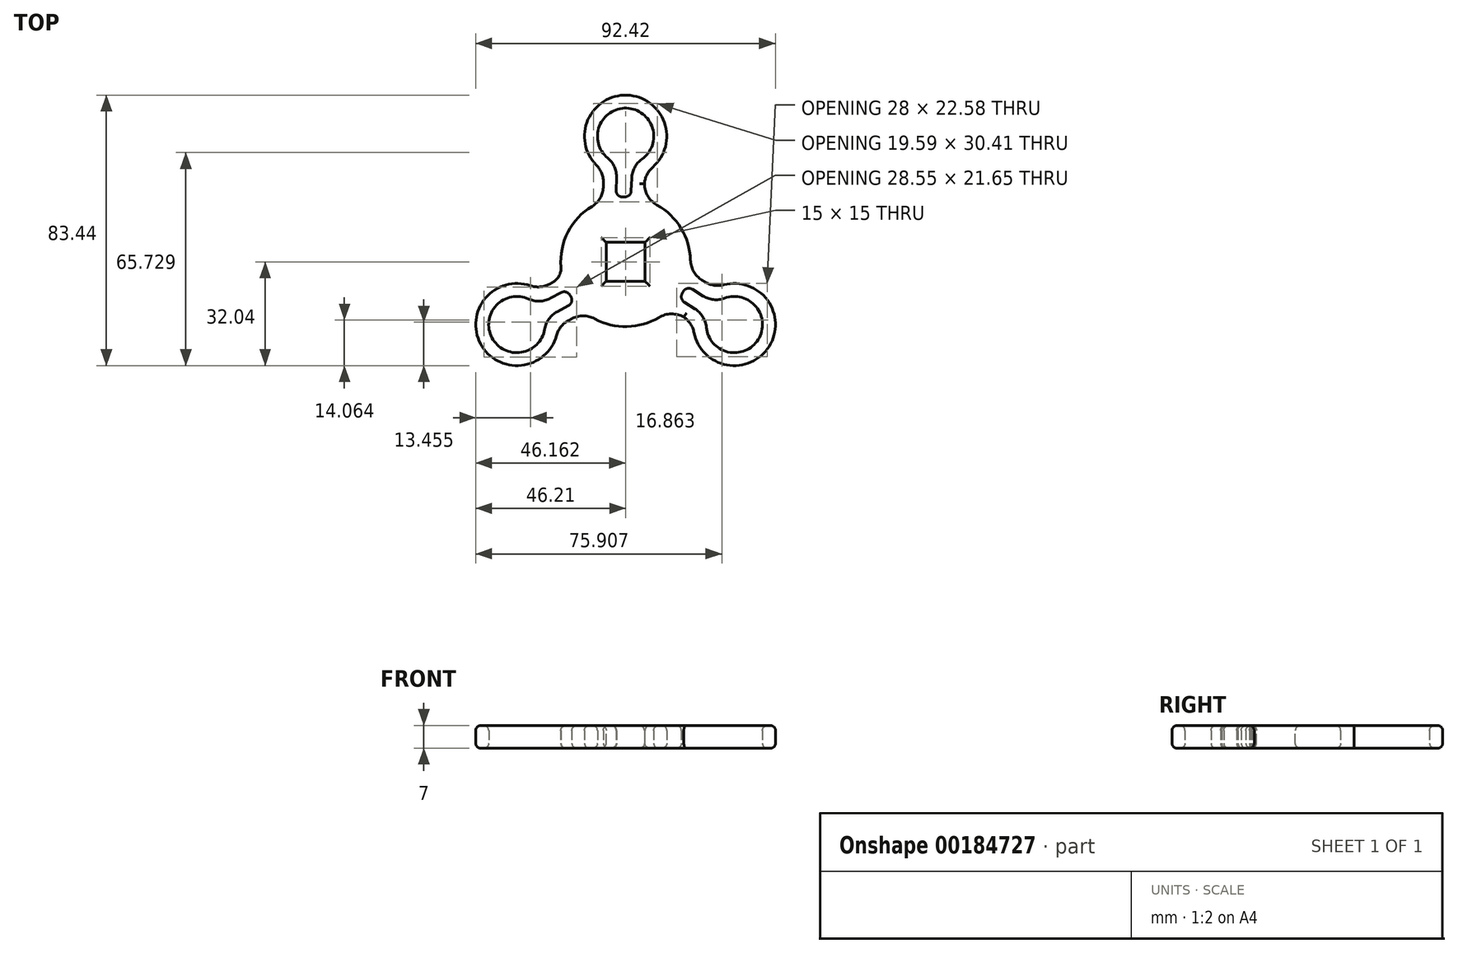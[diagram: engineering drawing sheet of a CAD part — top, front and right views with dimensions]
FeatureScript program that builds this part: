
annotation { "Feature Type Name" : "Feature", "Feature Type Description" : "" }
export const myFeature = defineFeature(function(context is Context, id is Id, definition is map)
    precondition{}
    {
        {
            var Q0;
            Q0=qCreatedBy(makeId("Top.planeOp"),FACE);
            var sketch = newSketch(context, id + "F0", { "sketchPlane" : qUnion([Q0])});
            skLineSegment(sketch, "E0.bottom", {"start": v(6, 6) * mm, "end": v(-6, 6) * mm});
            skLineSegment(sketch, "E0.top", {"start": v(6, -6) * mm, "end": v(-6, -6) * mm});
            skLineSegment(sketch, "E0.left", {"start": v(6, 6) * mm, "end": v(6, -6) * mm});
            skLineSegment(sketch, "E0.right", {"start": v(-6, 6) * mm, "end": v(-6, -6) * mm});
            skPoint(sketch, "E0.middle", {"position": v(0, 0) * mm});
            skLineSegment(sketch, "E1", {"start": v(0, 6) * mm, "end": v(0, 6.1) * mm, "construction": true});
            skLineSegment(sketch, "E2", {"start": v(9, 61.91) * mm, "end": v(9, 61.91) * mm});
            skLineSegment(sketch, "E3.MirrorCS", {"start": v(-9, 61.91) * mm, "end": v(-9, 61.91) * mm});
            skArc(sketch, "E4", {"start": v(-17.19, -10.22) * mm, "mid": v(-17.04, -10.48) * mm, "end": v(-16.88, -10.73) * mm});
            skLineSegment(sketch, "E5.left", {"start": v(-6.9, 22.9) * mm, "end": v(-6.86, 24.22) * mm});
            skLineSegment(sketch, "E5.right", {"start": v(5.78, 23.76) * mm, "end": v(5.8, 24.41) * mm});
            skArc(sketch, "E6", {"start": v(8.37, 29.2) * mm, "mid": v(0.46, 51.4) * mm, "end": v(-9.04, 29.83) * mm});
            skLineSegment(sketch, "E7.trimOffspring", {"start": v(0, 6.1) * mm, "end": v(0, 6) * mm, "construction": true});
            skLineSegment(sketch, "E8.0", {"start": v(1.71, 21.93) * mm, "end": v(1.85, 25.74) * mm});
            skArc(sketch, "E8.1", {"start": v(5.04, 31.66) * mm, "mid": v(0.32, 47.4) * mm, "end": v(-5.54, 32.04) * mm});
            skLineSegment(sketch, "E8.2", {"start": v(-2.94, 22.05) * mm, "end": v(-2.8, 25.9) * mm});
            skLineSegment(sketch, "E9.1.0", {"start": v(-17.63, -13.57) * mm, "end": v(-21.04, -15.37) * mm});
            skArc(sketch, "E9.1.1", {"start": v(-29.47, -7.35) * mm, "mid": v(-44.74, -25.3) * mm, "end": v(-21.32, -22.74) * mm});
            skLineSegment(sketch, "E9.1.2", {"start": v(-22.58, -6.4) * mm, "end": v(-23.46, -6.87) * mm});
            skArc(sketch, "E9.1.6", {"start": v(-29.94, -11.46) * mm, "mid": v(-41.2, -23.42) * mm, "end": v(-24.98, -20.82) * mm});
            skLineSegment(sketch, "E9.1.7", {"start": v(-19.84, -9.48) * mm, "end": v(-23.22, -11.26) * mm});
            skLineSegment(sketch, "E9.1.8", {"start": v(-16.66, -17.58) * mm, "end": v(-17.54, -18.05) * mm});
            skLineSegment(sketch, "E9.2.0", {"start": v(20.57, -8.48) * mm, "end": v(23.83, -10.53) * mm});
            skArc(sketch, "E9.2.1", {"start": v(21.1, -21.84) * mm, "mid": v(44.28, -26.1) * mm, "end": v(30.35, -7.09) * mm});
            skLineSegment(sketch, "E9.2.2", {"start": v(17.68, -16.89) * mm, "end": v(18.24, -17.23) * mm});
            skArc(sketch, "E9.2.6", {"start": v(24.9, -20.2) * mm, "mid": v(40.89, -23.97) * mm, "end": v(30.52, -11.22) * mm});
            skLineSegment(sketch, "E9.2.7", {"start": v(18.13, -12.45) * mm, "end": v(21.36, -14.47) * mm});
            skLineSegment(sketch, "E9.2.8", {"start": v(23.56, -5.64) * mm, "end": v(24.4, -6.17) * mm});
            skArc(sketch, "E10.trimOffspring", {"start": v(-9.49, -17.6) * mm, "mid": v(0.46, -20) * mm, "end": v(10.28, -17.15) * mm});
            skArc(sketch, "E11.trimOffspring", {"start": v(17.45, -9.77) * mm, "mid": v(17.6, -9.52) * mm, "end": v(17.73, -9.25) * mm});
            skArc(sketch, "E12.trimOffspring", {"start": v(20, 0.59) * mm, "mid": v(17.09, 10.4) * mm, "end": v(9.72, 17.48) * mm});
            skArc(sketch, "E13.trimOffspring", {"start": v(-0.26, 20) * mm, "mid": v(-0.56, 20) * mm, "end": v(-0.85, 19.98) * mm});
            skArc(sketch, "E14.trimOffspring", {"start": v(-10.3, 17.14) * mm, "mid": v(-17.78, 9.15) * mm, "end": v(-19.94, -1.59) * mm});
            skArc(sketch, "E15.filletArc", {"start": v(-10.3, 17.14) * mm, "mid": v(-7.87, 19.59) * mm, "end": v(-6.9, 22.9) * mm});
            skArc(sketch, "E16.filletArc", {"start": v(5.8, 24.41) * mm, "mid": v(6.78, 20.4) * mm, "end": v(9.72, 17.48) * mm});
            skArc(sketch, "E17.filletArc", {"start": v(20, 0.59) * mm, "mid": v(21, -2.97) * mm, "end": v(23.56, -5.64) * mm});
            skArc(sketch, "E18.filletArc", {"start": v(18.24, -17.23) * mm, "mid": v(14.27, -16.07) * mm, "end": v(10.28, -17.15) * mm});
            skArc(sketch, "E19.filletArc", {"start": v(-9.49, -17.6) * mm, "mid": v(-13.07, -16.7) * mm, "end": v(-16.66, -17.58) * mm});
            skArc(sketch, "E20.filletArc", {"start": v(-22.58, -6.4) * mm, "mid": v(-20.54, -4.39) * mm, "end": v(-19.94, -1.59) * mm});
            skArc(sketch, "E21.filletArc", {"start": v(-17.54, -18.05) * mm, "mid": v(-19.91, -20) * mm, "end": v(-21.32, -22.74) * mm});
            skArc(sketch, "E22.filletArc", {"start": v(-29.47, -7.35) * mm, "mid": v(-26.42, -7.73) * mm, "end": v(-23.46, -6.87) * mm});
            skArc(sketch, "E23.filletArc", {"start": v(21.1, -21.84) * mm, "mid": v(19.9, -19.01) * mm, "end": v(17.68, -16.89) * mm});
            skArc(sketch, "E24.filletArc", {"start": v(24.4, -6.17) * mm, "mid": v(27.28, -7.24) * mm, "end": v(30.35, -7.09) * mm});
            skArc(sketch, "E25.filletArc", {"start": v(24.9, -20.2) * mm, "mid": v(23.8, -16.92) * mm, "end": v(21.36, -14.47) * mm});
            skArc(sketch, "E26.filletArc", {"start": v(23.83, -10.53) * mm, "mid": v(27.1, -11.66) * mm, "end": v(30.52, -11.22) * mm});
            skArc(sketch, "E27.filletArc", {"start": v(5.04, 31.66) * mm, "mid": v(2.76, 29.07) * mm, "end": v(1.85, 25.74) * mm});
            skArc(sketch, "E28.filletArc", {"start": v(8.37, 29.2) * mm, "mid": v(6.51, 26.74) * mm, "end": v(5.78, 23.76) * mm});
            skArc(sketch, "E29.filletArc", {"start": v(-6.86, 24.22) * mm, "mid": v(-7.37, 27.25) * mm, "end": v(-9.04, 29.83) * mm});
            skArc(sketch, "E30.filletArc", {"start": v(-2.8, 25.9) * mm, "mid": v(-3.45, 29.3) * mm, "end": v(-5.54, 32.04) * mm});
            skArc(sketch, "E31.filletArc", {"start": v(-21.04, -15.37) * mm, "mid": v(-23.64, -17.64) * mm, "end": v(-24.98, -20.82) * mm});
            skArc(sketch, "E32.filletArc", {"start": v(-29.94, -11.46) * mm, "mid": v(-26.55, -12.15) * mm, "end": v(-23.22, -11.26) * mm});
            skArc(sketch, "E33.filletArc", {"start": v(-2.94, 22.05) * mm, "mid": v(-2.35, 20.56) * mm, "end": v(-0.85, 19.98) * mm});
            skArc(sketch, "E34.filletArc", {"start": v(-0.26, 20) * mm, "mid": v(1.11, 20.57) * mm, "end": v(1.71, 21.93) * mm});
            skArc(sketch, "E35.filletArc", {"start": v(20.57, -8.48) * mm, "mid": v(18.98, -8.25) * mm, "end": v(17.73, -9.25) * mm});
            skArc(sketch, "E36.filletArc", {"start": v(17.45, -9.77) * mm, "mid": v(17.26, -11.25) * mm, "end": v(18.13, -12.45) * mm});
            skArc(sketch, "E37.filletArc", {"start": v(-17.63, -13.57) * mm, "mid": v(-16.63, -12.31) * mm, "end": v(-16.88, -10.73) * mm});
            skArc(sketch, "E38.filletArc", {"start": v(-17.19, -10.22) * mm, "mid": v(-18.37, -9.32) * mm, "end": v(-19.84, -9.48) * mm});
            skLineSegment(sketch, "E39.trimOffspring", {"start": v(0, -20) * mm, "end": v(0, -71.78) * mm, "construction": true});
            skSolve(sketch);
        }
        {
            var Q0;
            Q0=makeQuery(id+"F0.imprint","IMPRINT",FACE,{"disambiguationData":[TD([[makeQuery(id+"F0.imprint","IMPRINT",EDGE,{"derivedFrom":sQuery(id+"F0.wireOp",EDGE,"E0.bottom")}),-1.0]])]});
            var sketch = newSketch(context, id + "F1", { "sketchPlane" : qUnion([Q0])});
            skLineSegment(sketch, "E40.0.0", {"start": v(-6.86, 24.22) * mm, "end": v(-6.9, 22.9) * mm});
            skArc(sketch, "E40.0.1", {"start": v(-6.9, 22.9) * mm, "mid": v(-7.87, 19.59) * mm, "end": v(-10.3, 17.14) * mm});
            skArc(sketch, "E40.0.2", {"start": v(-10.3, 17.14) * mm, "mid": v(-17.78, 9.15) * mm, "end": v(-19.94, -1.59) * mm});
            skArc(sketch, "E40.0.3", {"start": v(-19.94, -1.59) * mm, "mid": v(-20.54, -4.39) * mm, "end": v(-22.58, -6.4) * mm});
            skLineSegment(sketch, "E40.0.4", {"start": v(-22.58, -6.4) * mm, "end": v(-23.46, -6.87) * mm});
            skArc(sketch, "E40.0.5", {"start": v(-23.46, -6.87) * mm, "mid": v(-26.42, -7.73) * mm, "end": v(-29.47, -7.35) * mm});
            skArc(sketch, "E40.0.6", {"start": v(-29.47, -7.35) * mm, "mid": v(-44.74, -25.3) * mm, "end": v(-21.32, -22.74) * mm});
            skArc(sketch, "E40.0.7", {"start": v(-21.32, -22.74) * mm, "mid": v(-19.91, -20) * mm, "end": v(-17.54, -18.05) * mm});
            skLineSegment(sketch, "E40.0.8", {"start": v(-17.54, -18.05) * mm, "end": v(-16.66, -17.58) * mm});
            skArc(sketch, "E40.0.9", {"start": v(-16.66, -17.58) * mm, "mid": v(-13.07, -16.7) * mm, "end": v(-9.49, -17.6) * mm});
            skArc(sketch, "E40.0.10", {"start": v(-9.49, -17.6) * mm, "mid": v(0.46, -20) * mm, "end": v(10.28, -17.15) * mm});
            skArc(sketch, "E40.0.11", {"start": v(10.28, -17.15) * mm, "mid": v(14.1, -16.07) * mm, "end": v(17.96, -17.07) * mm});
            skArc(sketch, "E40.0.12", {"start": v(17.96, -17.07) * mm, "mid": v(17.82, -16.97) * mm, "end": v(17.68, -16.89) * mm});
            skLineSegment(sketch, "E40.0.13", {"start": v(17.68, -16.89) * mm, "end": v(18.24, -17.23) * mm});
            skArc(sketch, "E40.0.14", {"start": v(18.24, -17.23) * mm, "mid": v(18.1, -17.15) * mm, "end": v(17.96, -17.07) * mm});
            skArc(sketch, "E40.0.15", {"start": v(17.96, -17.07) * mm, "mid": v(20, -19.15) * mm, "end": v(21.1, -21.84) * mm});
            skArc(sketch, "E40.0.16", {"start": v(21.1, -21.84) * mm, "mid": v(44.28, -26.1) * mm, "end": v(30.35, -7.09) * mm});
            skArc(sketch, "E40.0.17", {"start": v(30.35, -7.09) * mm, "mid": v(27.28, -7.24) * mm, "end": v(24.4, -6.17) * mm});
            skLineSegment(sketch, "E40.0.18", {"start": v(24.4, -6.17) * mm, "end": v(23.56, -5.64) * mm});
            skArc(sketch, "E40.0.19", {"start": v(23.56, -5.64) * mm, "mid": v(21, -2.97) * mm, "end": v(20, 0.59) * mm});
            skArc(sketch, "E40.0.20", {"start": v(20, 0.59) * mm, "mid": v(17.09, 10.4) * mm, "end": v(9.72, 17.48) * mm});
            skArc(sketch, "E40.0.21", {"start": v(9.72, 17.48) * mm, "mid": v(6.87, 20.25) * mm, "end": v(5.8, 24.08) * mm});
            skArc(sketch, "E40.0.22", {"start": v(5.8, 24.08) * mm, "mid": v(5.8, 23.92) * mm, "end": v(5.78, 23.76) * mm});
            skLineSegment(sketch, "E40.0.23", {"start": v(5.78, 23.76) * mm, "end": v(5.8, 24.41) * mm});
            skArc(sketch, "E40.0.24", {"start": v(5.8, 24.41) * mm, "mid": v(5.8, 24.25) * mm, "end": v(5.8, 24.08) * mm});
            skArc(sketch, "E40.0.25", {"start": v(5.8, 24.08) * mm, "mid": v(6.59, 26.89) * mm, "end": v(8.37, 29.2) * mm});
            skArc(sketch, "E40.0.26", {"start": v(8.37, 29.2) * mm, "mid": v(0.46, 51.4) * mm, "end": v(-9.04, 29.83) * mm});
            skArc(sketch, "E40.0.27", {"start": v(-9.04, 29.83) * mm, "mid": v(-7.37, 27.25) * mm, "end": v(-6.86, 24.22) * mm});
            skSolve(sketch);
        }
        {
            var Q0;
            Q0 = qSketchRegion(id + "F1", true);
            extrude(context, id + "F2", {"entities" : qUnion([Q0]), "depth" : 7 * mm});
        }
        {
            var Q0;
            Q0=makeQuery(id+"F2.opExtrude","CAP_FACE",FACE,{"disambiguationData":[OSD([sQuery(id+"F1.wireOp",EDGE,"E40.0.0"),sQuery(id+"F1.wireOp",EDGE,"E40.0.1"),sQuery(id+"F1.wireOp",EDGE,"E40.0.2"),sQuery(id+"F1.wireOp",EDGE,"E40.0.3"),sQuery(id+"F1.wireOp",EDGE,"E40.0.4"),sQuery(id+"F1.wireOp",EDGE,"E40.0.5"),sQuery(id+"F1.wireOp",EDGE,"E40.0.6"),sQuery(id+"F1.wireOp",EDGE,"E40.0.7"),sQuery(id+"F1.wireOp",EDGE,"E40.0.8"),sQuery(id+"F1.wireOp",EDGE,"E40.0.9"),sQuery(id+"F1.wireOp",EDGE,"E40.0.10"),sQuery(id+"F1.wireOp",EDGE,"E40.0.11"),sQuery(id+"F1.wireOp",EDGE,"E40.0.15"),sQuery(id+"F1.wireOp",EDGE,"E40.0.16"),sQuery(id+"F1.wireOp",EDGE,"E40.0.17"),sQuery(id+"F1.wireOp",EDGE,"E40.0.18"),sQuery(id+"F1.wireOp",EDGE,"E40.0.19"),sQuery(id+"F1.wireOp",EDGE,"E40.0.20"),sQuery(id+"F1.wireOp",EDGE,"E40.0.21"),sQuery(id+"F1.wireOp",EDGE,"E40.0.25"),sQuery(id+"F1.wireOp",EDGE,"E40.0.26"),sQuery(id+"F1.wireOp",EDGE,"E40.0.27")])],"isStart":false});
            var sketch = newSketch(context, id + "F3", { "sketchPlane" : qUnion([Q0])});
            skLineSegment(sketch, "E41.bottom", {"start": v(6, 6) * mm, "end": v(-6, 6) * mm});
            skLineSegment(sketch, "E41.top", {"start": v(6, -6) * mm, "end": v(-6, -6) * mm});
            skLineSegment(sketch, "E41.left", {"start": v(6, 6) * mm, "end": v(6, -6) * mm});
            skLineSegment(sketch, "E41.right", {"start": v(-6, 6) * mm, "end": v(-6, -6) * mm});
            skPoint(sketch, "E41.middle", {"position": v(0, 0) * mm});
            skSolve(sketch);
        }
        {
            var Q0;
            Q0 = qSketchRegion(id + "F3", true);
            extrude(context, id + "F4", {"entities" : qUnion([Q0]), "operationType" : NewBodyOperationType.REMOVE, "endBound" : BoundingType.THROUGH_ALL, "oppositeDirection" : true, "depth" : 25 * mm});
        }
        {
            var Q0;
            Q0=makeQuery(id+"F0.imprint","IMPRINT",FACE,{"disambiguationData":[TD([[makeQuery(id+"F0.imprint","IMPRINT",EDGE,{"derivedFrom":sQuery(id+"F0.wireOp",EDGE,"E9.2.0")}),-1.0]])]});
            var Q1;
            Q1=makeQuery(id+"F0.imprint","IMPRINT",FACE,{"disambiguationData":[TD([[makeQuery(id+"F0.imprint","IMPRINT",EDGE,{"derivedFrom":sQuery(id+"F0.wireOp",EDGE,"E8.0")}),1.0]])]});
            var Q2;
            Q2=makeQuery(id+"F0.imprint","IMPRINT",FACE,{"disambiguationData":[TD([[makeQuery(id+"F0.imprint","IMPRINT",EDGE,{"derivedFrom":sQuery(id+"F0.wireOp",EDGE,"E4")}),-1.0]])]});
            extrude(context, id + "F5", {"entities" : qUnion([Q0, Q1, Q2]), "operationType" : NewBodyOperationType.REMOVE, "depth" : 10 * mm});
        }
        {
            var Q0;
            Q0=makeQuery(id+"F2.opExtrude","CAP_FACE",FACE,{"disambiguationData":[OSD([sQuery(id+"F1.wireOp",EDGE,"E40.0.0"),sQuery(id+"F1.wireOp",EDGE,"E40.0.1"),sQuery(id+"F1.wireOp",EDGE,"E40.0.2"),sQuery(id+"F1.wireOp",EDGE,"E40.0.3"),sQuery(id+"F1.wireOp",EDGE,"E40.0.4"),sQuery(id+"F1.wireOp",EDGE,"E40.0.5"),sQuery(id+"F1.wireOp",EDGE,"E40.0.6"),sQuery(id+"F1.wireOp",EDGE,"E40.0.7"),sQuery(id+"F1.wireOp",EDGE,"E40.0.8"),sQuery(id+"F1.wireOp",EDGE,"E40.0.9"),sQuery(id+"F1.wireOp",EDGE,"E40.0.10"),sQuery(id+"F1.wireOp",EDGE,"E40.0.11"),sQuery(id+"F1.wireOp",EDGE,"E40.0.15"),sQuery(id+"F1.wireOp",EDGE,"E40.0.16"),sQuery(id+"F1.wireOp",EDGE,"E40.0.17"),sQuery(id+"F1.wireOp",EDGE,"E40.0.18"),sQuery(id+"F1.wireOp",EDGE,"E40.0.19"),sQuery(id+"F1.wireOp",EDGE,"E40.0.20"),sQuery(id+"F1.wireOp",EDGE,"E40.0.21"),sQuery(id+"F1.wireOp",EDGE,"E40.0.25"),sQuery(id+"F1.wireOp",EDGE,"E40.0.26"),sQuery(id+"F1.wireOp",EDGE,"E40.0.27")])],"isStart":false});
            var Q1;
            Q1=makeQuery(id+"F2.opExtrude","CAP_EDGE",EDGE,{"disambiguationData":[OSD([sQuery(id+"F1.wireOp",EDGE,"E40.0.26")])],"isStart":false});
            var Q2;
            Q2=makeQuery(id+"F2.opExtrude","CAP_EDGE",EDGE,{"disambiguationData":[OSD([sQuery(id+"F1.wireOp",EDGE,"E40.0.2")])],"isStart":false});
            var Q3;
            Q3=makeQuery(id+"F2.opExtrude","CAP_EDGE",EDGE,{"disambiguationData":[OSD([sQuery(id+"F1.wireOp",EDGE,"E40.0.2")])],"isStart":true});
            var Q4;
            Q4=makeQuery(id+"F2.opExtrude","CAP_FACE",FACE,{"disambiguationData":[OSD([sQuery(id+"F1.wireOp",EDGE,"E40.0.0"),sQuery(id+"F1.wireOp",EDGE,"E40.0.1"),sQuery(id+"F1.wireOp",EDGE,"E40.0.2"),sQuery(id+"F1.wireOp",EDGE,"E40.0.3"),sQuery(id+"F1.wireOp",EDGE,"E40.0.4"),sQuery(id+"F1.wireOp",EDGE,"E40.0.5"),sQuery(id+"F1.wireOp",EDGE,"E40.0.6"),sQuery(id+"F1.wireOp",EDGE,"E40.0.7"),sQuery(id+"F1.wireOp",EDGE,"E40.0.8"),sQuery(id+"F1.wireOp",EDGE,"E40.0.9"),sQuery(id+"F1.wireOp",EDGE,"E40.0.10"),sQuery(id+"F1.wireOp",EDGE,"E40.0.11"),sQuery(id+"F1.wireOp",EDGE,"E40.0.15"),sQuery(id+"F1.wireOp",EDGE,"E40.0.16"),sQuery(id+"F1.wireOp",EDGE,"E40.0.17"),sQuery(id+"F1.wireOp",EDGE,"E40.0.18"),sQuery(id+"F1.wireOp",EDGE,"E40.0.19"),sQuery(id+"F1.wireOp",EDGE,"E40.0.20"),sQuery(id+"F1.wireOp",EDGE,"E40.0.21"),sQuery(id+"F1.wireOp",EDGE,"E40.0.25"),sQuery(id+"F1.wireOp",EDGE,"E40.0.26"),sQuery(id+"F1.wireOp",EDGE,"E40.0.27")])],"isStart":true});
            fillet(context, id + "F6", {"entities" : qUnion([Q0, Q1, Q2, Q3, Q4]), "radius" : 1.5 * mm, "tangentPropagation" : true, "allowEdgeOverflow" : false});
        }
    });
